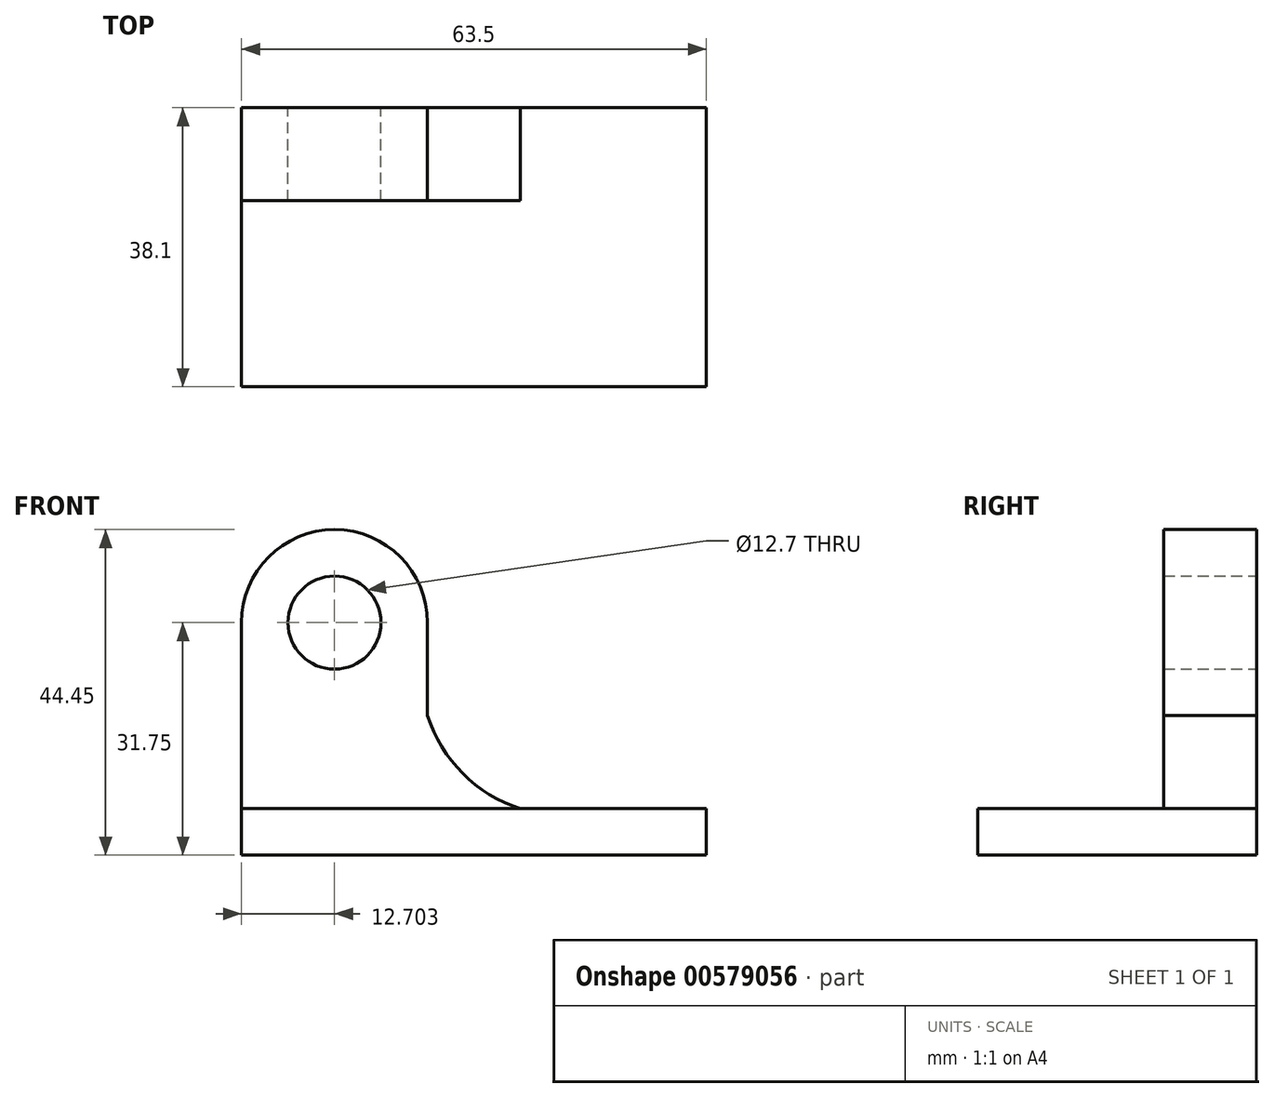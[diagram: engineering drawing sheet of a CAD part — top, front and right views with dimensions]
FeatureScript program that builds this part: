
annotation { "Feature Type Name" : "Feature", "Feature Type Description" : "" }
export const myFeature = defineFeature(function(context is Context, id is Id, definition is map)
    precondition{}
    {
        {
            var Q0;
            Q0=qCreatedBy(makeId("Front.planeOp"),FACE);
            var sketch = newSketch(context, id + "F0", { "sketchPlane" : qUnion([Q0])});
            skLineSegment(sketch, "E0", {"start": v(-88.04, 25.52) * mm, "end": v(-88.04, -6.23) * mm});
            skLineSegment(sketch, "E1", {"start": v(-88.04, -6.23) * mm, "end": v(-24.54, -6.23) * mm});
            skLineSegment(sketch, "E2", {"start": v(-24.54, -6.23) * mm, "end": v(-24.54, 0.12) * mm});
            skLineSegment(sketch, "E3", {"start": v(-24.54, 0.12) * mm, "end": v(-62.64, 0.12) * mm});
            skLineSegment(sketch, "E4", {"start": v(-62.64, 0.12) * mm, "end": v(-62.64, 25.52) * mm});
            skLineSegment(sketch, "E5", {"start": v(-62.64, 25.52) * mm, "end": v(-88.04, 25.52) * mm});
            skArc(sketch, "E6", {"start": v(-62.64, 25.52) * mm, "mid": v(-75.34, 38.22) * mm, "end": v(-88.04, 25.52) * mm});
            skCircle(sketch, "E7", {"center": v(-75.34, 25.52) * mm, "radius": 6.35 * mm});
            skLineSegment(sketch, "E8", {"start": v(-62.64, 0.12) * mm, "end": v(-62.64, -6.23) * mm});
            skArc(sketch, "E9", {"start": v(-62.64, 12.82) * mm, "mid": v(-57.82, 4.94) * mm, "end": v(-49.94, 0.12) * mm});
            skSolve(sketch);
        }
        {
            var Q0;
            {var subQ0=sQuery(id+"F0.wireOp",EDGE,"E6");Q0=makeQuery(id+"F0.imprint","IMPRINT",FACE,{"disambiguationData":[TD([[makeQuery(id+"F0.imprint","IMPRINT",EDGE,{"derivedFrom":subQ0}),1.0]])]});}
            var Q1;
            {var subQ6=sQuery(id+"F0.wireOp",EDGE,"E0");Q1=makeQuery(id+"F0.imprint","IMPRINT",FACE,{"disambiguationData":[TD([[makeQuery(id+"F0.imprint","IMPRINT",EDGE,{"derivedFrom":subQ6}),1.0]])]});}
            extrude(context, id + "F1", {"entities" : qUnion([Q0, Q1]), "depth" : 12.7 * mm, "offsetDistance" : 25.4 * mm});
        }
        {
            var Q0;
            Q0 = qSketchRegion(id + "F0", true);
            extrude(context, id + "F2", {"entities" : qUnion([Q0]), "operationType" : NewBodyOperationType.ADD, "depth" : 12.7 * mm, "offsetDistance" : 25.4 * mm});
        }
        {
            var Q0;
            {var subQ0=sQuery(id+"F0.wireOp",EDGE,"E7");var subQ1=sQuery(id+"F0.wireOp",EDGE,"E6");var subQ2=sQuery(id+"F0.wireOp",EDGE,"E4");var subQ3=sQuery(id+"F0.wireOp",EDGE,"E1");var subQ4=sQuery(id+"F0.wireOp",EDGE,"E0");Q0=makeQuery(id+"F2.boolean.opBoolean","MERGE",FACE,{"derivedFrom":[makeQuery(id+"F1.opExtrude","CAP_FACE",FACE,{"disambiguationData":[OSD([subQ4,subQ3,subQ2,subQ1,subQ0,sQuery(id+"F0.wireOp",EDGE,"E8")])],"isStart":false}),makeQuery(id+"F2.opExtrude","CAP_FACE",FACE,{"disambiguationData":[OSD([subQ4,subQ3,sQuery(id+"F0.wireOp",EDGE,"E2"),sQuery(id+"F0.wireOp",EDGE,"E3"),subQ2,subQ1,subQ0])],"isStart":false})]});}
            var sketch = newSketch(context, id + "F3", { "sketchPlane" : qUnion([Q0])});
            skLineSegment(sketch, "E10", {"start": v(-24.54, 0.12) * mm, "end": v(-24.54, -6.23) * mm});
            skLineSegment(sketch, "E11", {"start": v(-24.54, 0.12) * mm, "end": v(-88.04, 0.12) * mm});
            skSolve(sketch);
        }
        {
            var Q0;
            {var subQ0=sQuery(id+"F3.wireOp",EDGE,"E10");Q0=makeQuery(id+"F3.imprint","IMPRINT",FACE,{"disambiguationData":[TD([[makeQuery(id+"F3.imprint","IMPRINT",EDGE,{"derivedFrom":subQ0}),1.0]])]});}
            var Q1;
            {var subQ0=sQuery(id+"F3.wireOp",EDGE,"E10");Q1=makeQuery(id+"F3.imprint","IMPRINT",FACE,{"disambiguationData":[TD([[makeQuery(id+"F3.imprint","IMPRINT",EDGE,{"derivedFrom":subQ0}),-1.0]])]});}
            extrude(context, id + "F4", {"entities" : qUnion([Q0, Q1]), "operationType" : NewBodyOperationType.ADD, "depth" : 25.4 * mm, "offsetDistance" : 25.4 * mm});
        }
    });
